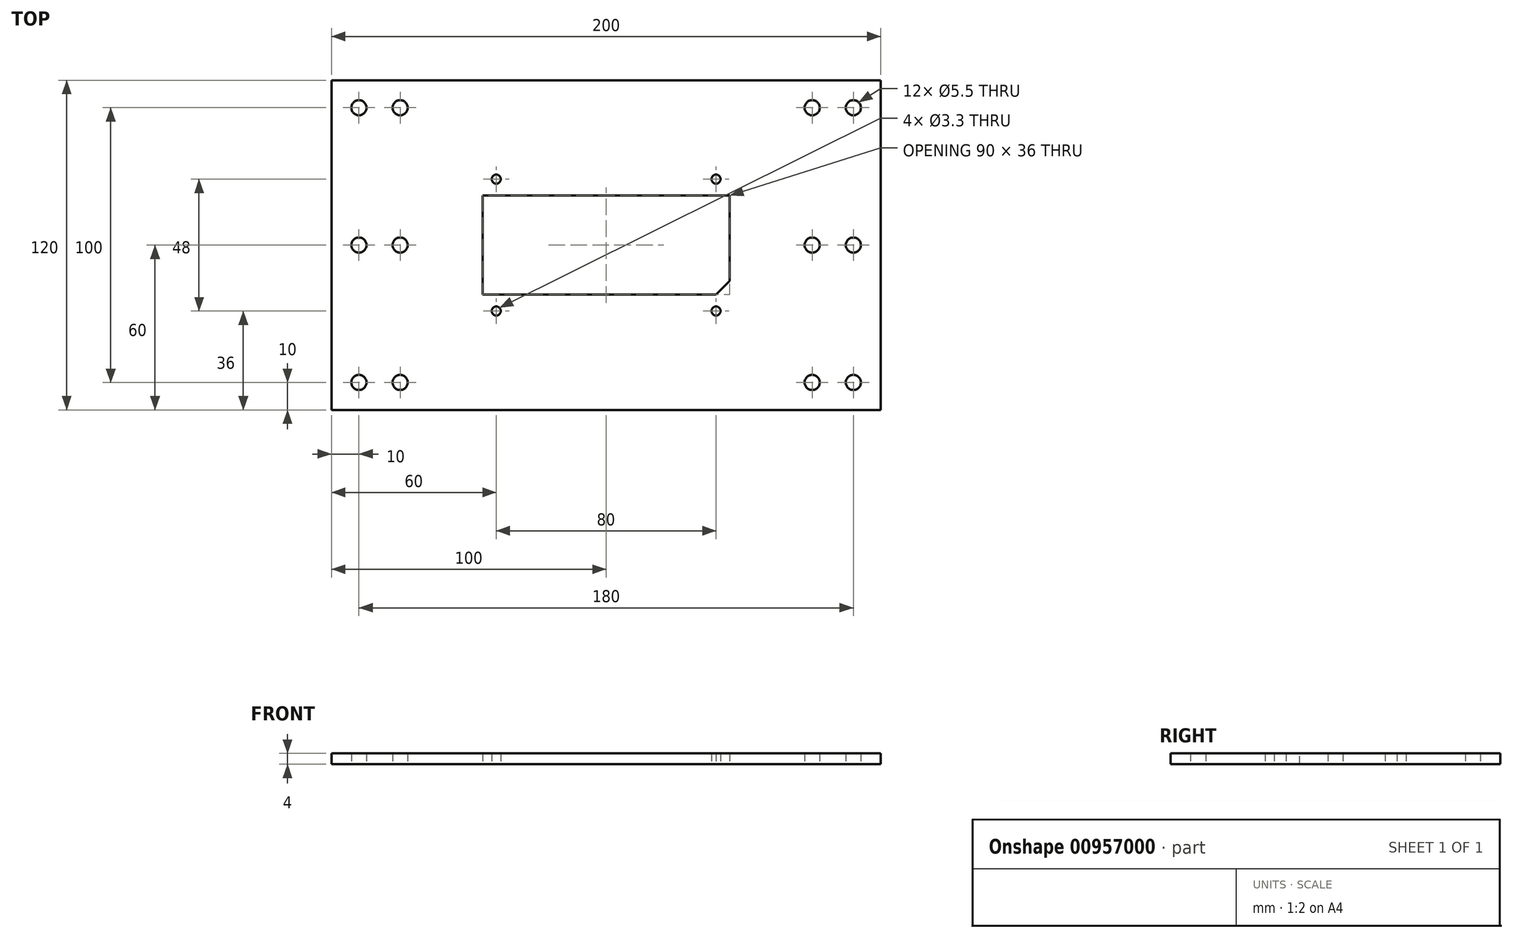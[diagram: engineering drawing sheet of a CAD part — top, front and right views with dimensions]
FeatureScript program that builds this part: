
annotation { "Feature Type Name" : "Feature", "Feature Type Description" : "" }
export const myFeature = defineFeature(function(context is Context, id is Id, definition is map)
    precondition{}
    {
        {
            assignVariable(context, id + "F0", {"name" : "thickness", "anyValue" : 4});
        }
        {
            var Q0;
            Q0=qCreatedBy(makeId("Top.planeOp"),FACE);
            var sketch = newSketch(context, id + "F1", { "sketchPlane" : qUnion([Q0])});
            skLineSegment(sketch, "E0.bottom", {"start": v(0, 120) * mm, "end": v(200, 120) * mm});
            skLineSegment(sketch, "E0.top", {"start": v(0, 0) * mm, "end": v(200, 0) * mm});
            skLineSegment(sketch, "E0.left", {"start": v(0, 120) * mm, "end": v(0, 0) * mm});
            skLineSegment(sketch, "E0.right", {"start": v(200, 120) * mm, "end": v(200, 0) * mm});
            skSolve(sketch);
        }
        {
            var Q0;
            Q0 = qSketchRegion(id + "F1", true);
            extrude(context, id + "F2", {"entities" : qUnion([Q0]), "depth" : (getVariable(context, 'thickness')) * mm, "offsetDistance" : 25 * mm});
        }
        {
            var Q0;
            Q0=qCreatedBy(makeId("Top.planeOp"),FACE);
            var sketch = newSketch(context, id + "F3", { "sketchPlane" : qUnion([Q0])});
            skLineSegment(sketch, "E1.bottom", {"start": v(55, 78) * mm, "end": v(145, 78) * mm});
            skLineSegment(sketch, "E1.top", {"start": v(55, 42) * mm, "end": v(145, 42) * mm});
            skLineSegment(sketch, "E1.left", {"start": v(55, 78) * mm, "end": v(55, 42) * mm});
            skLineSegment(sketch, "E1.right", {"start": v(145, 78) * mm, "end": v(145, 42) * mm});
            skSolve(sketch);
        }
        {
            var Q0;
            Q0 = qSketchRegion(id + "F3", true);
            var Q1;
            Q1=makeQuery(id+"F2.opExtrude","CAP_FACE",FACE,{"disambiguationData":[OSD([sQuery(id+"F1.wireOp",EDGE,"E0.bottom"),sQuery(id+"F1.wireOp",EDGE,"E0.top"),sQuery(id+"F1.wireOp",EDGE,"E0.left"),sQuery(id+"F1.wireOp",EDGE,"E0.right")])],"isStart":false});
            extrude(context, id + "F4", {"entities" : qUnion([Q0]), "operationType" : NewBodyOperationType.REMOVE, "endBound" : BoundingType.UP_TO_SURFACE, "depth" : 25 * mm, "endBoundEntityFace" : qUnion([Q1]), "offsetDistance" : 25 * mm});
        }
        {
            var Q0;
            Q0=makeQuery(id+"F4.boolean.opBoolean","COPY",EDGE,{"derivedFrom":makeQuery(id+"F4.opExtrude","SWEPT_EDGE",EDGE,{"disambiguationData":[OSD([sQuery(id+"F3.wireOp",EDGE,"E1.top"),sQuery(id+"F3.wireOp",EDGE,"E1.right")])]})});
            chamfer(context, id + "F5", {"entities" : qUnion([Q0]), "width" : 5 * mm, "tangentPropagation" : true});
        }
        {
            var Q0;
            Q0=qCreatedBy(makeId("Top.planeOp"),FACE);
            var sketch = newSketch(context, id + "F6", { "sketchPlane" : qUnion([Q0])});
            skPoint(sketch, "E2", {"position": v(60, 84) * mm});
            skPoint(sketch, "E3", {"position": v(60, 36) * mm});
            skPoint(sketch, "E4", {"position": v(140, 36) * mm});
            skPoint(sketch, "E5", {"position": v(140, 84) * mm});
            skSolve(sketch);
        }
        {
            var Q0;
            Q0=sQuery(id+"F6.wireOp",VERTEX,"E5");
            var Q1;
            Q1=sQuery(id+"F6.wireOp",VERTEX,"E4");
            var Q2;
            Q2=sQuery(id+"F6.wireOp",VERTEX,"E3");
            var Q3;
            Q3=sQuery(id+"F6.wireOp",VERTEX,"E2");
            var Q4;
            Q4=makeQuery(id+"F2.opExtrude","SWEPT_BODY",BODY,{"disambiguationData":[OSD([sQuery(id+"F1.wireOp",EDGE,"E0.bottom"),sQuery(id+"F1.wireOp",EDGE,"E0.top"),sQuery(id+"F1.wireOp",EDGE,"E0.left"),sQuery(id+"F1.wireOp",EDGE,"E0.right")])]});
            hole(context, id + "F7", {"style" : HoleStyle.SIMPLE, "endStyle" : HoleEndStyle.THROUGH, "oppositeDirection" : true, "standardTappedOrClearance" : lookupTablePath({ "standard" : "ISO", "engagement" : "75%", "pitch" : "0.7 mm", "size" : "M4", "type" : "Tapped" }), "standardBlindInLast" : lookupTablePath({ "standard" : "ISO", "fit" : "Normal", "engagement" : "75%", "pitch" : "0.7 mm", "size" : "M4", "type" : "Clearance & tapped" }), "holeDiameter" : 3.3 * mm, "majorDiameter" : 4 * mm, "showTappedDepth" : true, "isTappedThrough" : true, "tappedDepth" : 12 * mm, "tapClearance" : 3, "locations" : qUnion([Q0, Q1, Q2, Q3]), "scope" : qUnion([Q4])});
        }
        {
            var Q0;
            Q0=qCreatedBy(makeId("Top.planeOp"),FACE);
            var sketch = newSketch(context, id + "F8", { "sketchPlane" : qUnion([Q0])});
            skPoint(sketch, "E6", {"position": v(25, 10) * mm});
            skPoint(sketch, "E7", {"position": v(25, 60) * mm});
            skPoint(sketch, "E8", {"position": v(25, 110) * mm});
            skLineSegment(sketch, "E9", {"start": v(100, 120) * mm, "end": v(100, 0) * mm});
            skPoint(sketch, "E10.MirrorP", {"position": v(175, 110) * mm});
            skPoint(sketch, "E11.MirrorP", {"position": v(175, 60) * mm});
            skPoint(sketch, "E12.MirrorP", {"position": v(175, 10) * mm});
            skPoint(sketch, "E13.1.0.0", {"position": v(10, 110) * mm});
            skPoint(sketch, "E13.1.0.1", {"position": v(10, 60) * mm});
            skPoint(sketch, "E13.1.0.2", {"position": v(10, 10) * mm});
            skLineSegment(sketch, "E13.direction1", {"start": v(25, 110) * mm, "end": v(10, 110) * mm, "construction": true});
            skPoint(sketch, "E14.MirrorP", {"position": v(190, 60) * mm});
            skPoint(sketch, "E15.MirrorP", {"position": v(190, 10) * mm});
            skPoint(sketch, "E16.MirrorP", {"position": v(190, 110) * mm});
            skSolve(sketch);
        }
        {
            var Q0;
            Q0=sQuery(id+"F8.wireOp",VERTEX,"E8");
            var Q1;
            Q1=sQuery(id+"F8.wireOp",VERTEX,"E7");
            var Q2;
            Q2=sQuery(id+"F8.wireOp",VERTEX,"E6");
            var Q3;
            Q3=sQuery(id+"F8.wireOp",VERTEX,"E10.MirrorP");
            var Q4;
            Q4=sQuery(id+"F8.wireOp",VERTEX,"E11.MirrorP");
            var Q5;
            Q5=sQuery(id+"F8.wireOp",VERTEX,"E12.MirrorP");
            var Q6;
            Q6=sQuery(id+"F8.wireOp",VERTEX,"E13.1.0.0");
            var Q7;
            Q7=sQuery(id+"F8.wireOp",VERTEX,"E13.1.0.1");
            var Q8;
            Q8=sQuery(id+"F8.wireOp",VERTEX,"E13.1.0.2");
            var Q9;
            Q9=sQuery(id+"F8.wireOp",VERTEX,"E16.MirrorP");
            var Q10;
            Q10=sQuery(id+"F8.wireOp",VERTEX,"E14.MirrorP");
            var Q11;
            Q11=sQuery(id+"F8.wireOp",VERTEX,"E15.MirrorP");
            var Q12;
            Q12=makeQuery(id+"F2.opExtrude","SWEPT_BODY",BODY,{"disambiguationData":[OSD([sQuery(id+"F1.wireOp",EDGE,"E0.bottom"),sQuery(id+"F1.wireOp",EDGE,"E0.top"),sQuery(id+"F1.wireOp",EDGE,"E0.left"),sQuery(id+"F1.wireOp",EDGE,"E0.right")])]});
            hole(context, id + "F9", {"style" : HoleStyle.SIMPLE, "endStyle" : HoleEndStyle.THROUGH, "oppositeDirection" : true, "standardTappedOrClearance" : lookupTablePath({ "standard" : "ISO", "size" : "5.5", "type" : "Drilled" }), "standardBlindInLast" : lookupTablePath({ "standard" : "ISO", "size" : "5.5", "type" : "Drilled" }), "holeDiameter" : 5.5 * mm, "majorDiameter" : 5 * mm, "isTappedThrough" : true, "tappedDepth" : 12 * mm, "tapClearance" : 3, "locations" : qUnion([Q0, Q1, Q2, Q3, Q4, Q5, Q6, Q7, Q8, Q9, Q10, Q11]), "scope" : qUnion([Q12])});
        }
    });
